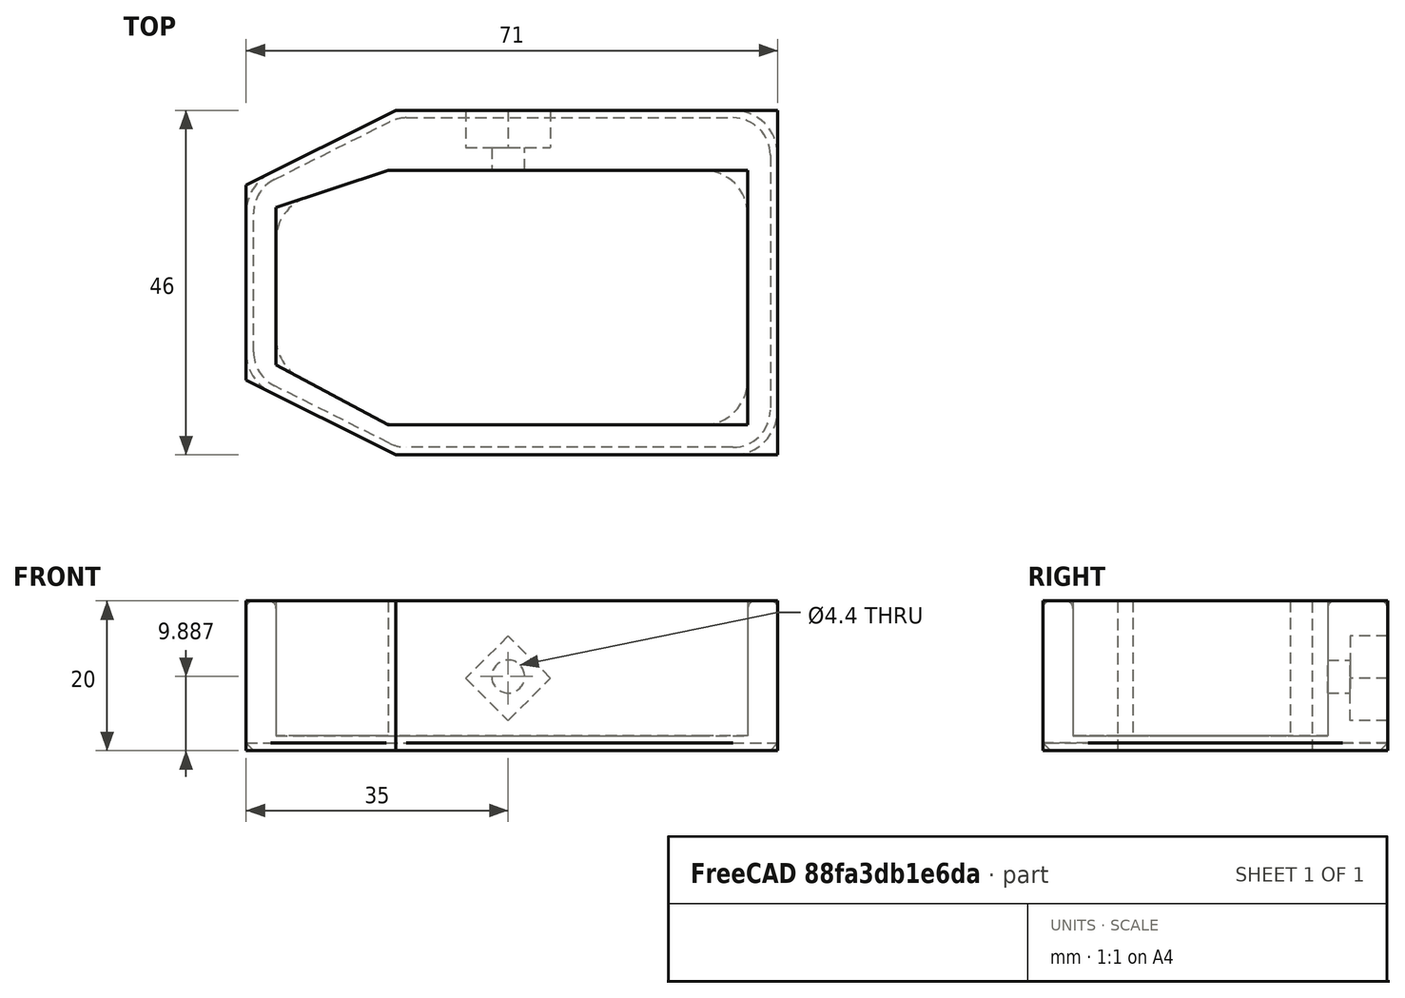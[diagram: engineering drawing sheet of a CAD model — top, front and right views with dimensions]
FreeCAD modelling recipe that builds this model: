
FCSTD DOCUMENT  (FreeCAD 0.16R)
Label: KetchupA
License: All rights reserved
LicenseURL: http://en.wikipedia.org/wiki/All_rights_reserved
objects: Sketcher::SketchObject×4, PartDesign::Pocket×3, PartDesign::Fillet×2, PartDesign::Pad×1, PartDesign::Chamfer×1, Mesh::Feature×1
note: 15 computed .brp shape members not serialized (recipe doc carries the construction recipe); baked Part::Feature solids carry a one-line shape summary decoded from their .brp

FEATURE [Sketcher::SketchObject] Sketch001
  sketch-geometry (6):
    g0: LineSegment StartX=-43 StartY=13 StartZ=0 EndX=-23 EndY=23 EndZ=0
    g1: LineSegment StartX=-23 StartY=23 StartZ=0 EndX=28 EndY=23 EndZ=0
    g2: LineSegment StartX=28 StartY=23 StartZ=0 EndX=28 EndY=-23 EndZ=0
    g3: LineSegment StartX=28 StartY=-23 StartZ=0 EndX=-23 EndY=-23 EndZ=0
    g4: LineSegment StartX=-23 StartY=-23 StartZ=0 EndX=-43 EndY=-13 EndZ=0
    g5: LineSegment StartX=-43 StartY=-13 StartZ=0 EndX=-43 EndY=13 EndZ=0
  constraints (18):
    c: Coincident(g0,g1)
    c: Horizontal(g1)
    c: Coincident(g1,g2)
    c: Vertical(g2)
    c: Coincident(g2,g3)
    c: Horizontal(g3)
    c: Coincident(g3,g4)
    c: Coincident(g4,g5)
    c: Coincident(g5,g0)
    c: Vertical(g5)
    c: Symmetric(g1,g2,g-1)
    c: Symmetric(g0,g4,g-1)
    c: DistanceX(g4) = -43
    c: DistanceX(g2) = 28
    c: Distance(g3,g0) = 46
    c: Equal(g1,g3)
    c: Distance(g5) = 26
    c: Distance(g3) = 51
FEATURE [PartDesign::Pad] Pad
  Length = 20
  Length2 = 100
  Sketch = -> Sketch001
  Type = 0
FEATURE [Sketcher::SketchObject] Sketch
  Placement = pos=(0,0,20) rot=(0,0,1;0rad)
  Support = -> Pad [Face8]
  sketch-geometry (6):
    g0: LineSegment StartX=-24 StartY=15 StartZ=0 EndX=24 EndY=15 EndZ=0
    g1: LineSegment StartX=24 StartY=15 StartZ=0 EndX=24 EndY=-19 EndZ=0
    g2: LineSegment StartX=24 StartY=-19 StartZ=0 EndX=-24 EndY=-19 EndZ=0
    g3: LineSegment StartX=-24 StartY=-19 StartZ=0 EndX=-39 EndY=-11 EndZ=0
    g4: LineSegment StartX=-39 StartY=-11 StartZ=0 EndX=-39 EndY=10 EndZ=0
    g5: LineSegment StartX=-39 StartY=10 StartZ=0 EndX=-24 EndY=15 EndZ=0
  constraints (18):
    c: Horizontal(g0)
    c: Coincident(g0,g1)
    c: Coincident(g1,g2)
    c: Horizontal(g2)
    c: Coincident(g2,g3)
    c: Coincident(g3,g4)
    c: Vertical(g4)
    c: Coincident(g4,g5)
    c: Coincident(g5,g0)
    c: Vertical(g1)
    c: Distance(g1) = 34
    c: Distance(g0) = 48
    c: Equal(g2,g0)
    c: DistanceX(g4,g0) = 15
    c: Distance(g4) = 21
    c: DistanceY(g1) = -19
    c: DistanceX(g1) = 24
    c: DistanceY(g3) = -11
FEATURE [PartDesign::Pocket] Pocket
  Length = 18
  Sketch = -> Sketch
  Type = 0
FEATURE [Sketcher::SketchObject] Sketch002
  Placement = pos=(0,23,0) rot=(0,0.707107,0.707107;3.14159rad)
  Support = -> Pocket [Face3]
  sketch-geometry (4):
    g0: LineSegment StartX=8.01225 StartY=15.3137 StartZ=0 EndX=13.6691 EndY=9.65685 EndZ=0
    g1: LineSegment StartX=13.6691 StartY=9.65685 StartZ=0 EndX=8.01225 EndY=4 EndZ=0
    g2: LineSegment StartX=8.01225 StartY=4 StartZ=0 EndX=2.3554 EndY=9.65685 EndZ=0
    g3: LineSegment StartX=2.3554 StartY=9.65685 StartZ=0 EndX=8.01225 EndY=15.3137 EndZ=0
  constraints (12):
    c: Coincident(g0,g1)
    c: Coincident(g1,g2)
    c: Coincident(g2,g3)
    c: Coincident(g3,g0)
    c: Equal(g1,g0)
    c: Distance(g1) = 8
    c: Equal(g3,g0)
    c: Equal(g1,g0)
    c: Perpendicular(g0,g3)
    c: Equal(g2,g1)
    c: DistanceY(g1) = 4
    c: Angle(g0) = -0.785398
FEATURE [PartDesign::Pocket] Pocket001
  Length = 5
  Sketch = -> Sketch002
  Type = 0
FEATURE [Sketcher::SketchObject] Sketch003
  Placement = pos=(0,18,0) rot=(0,0.707107,0.707107;3.14159rad)
  Support = -> Pocket001 [Face19]
  sketch-geometry (1):
    g0: Circle CenterX=8 CenterY=9.88737 CenterZ=0 NormalX=0 NormalY=0 NormalZ=1 Radius=2.2
  constraints (2):
    c: Radius(g0) = 2.2
    c: DistanceX(g0) = 8
FEATURE [PartDesign::Pocket] Pocket002
  Length = 5
  Sketch = -> Sketch003
  Type = 0
FEATURE [PartDesign::Fillet] Fillet
  Base = -> Pocket002 [Edge5,Edge1,Edge2,Edge41,Edge39,Edge37,Edge27,Edge28,Edge48,Edge45,Edge10,Edge43]
  Radius = 6
FEATURE [PartDesign::Fillet] Fillet001
  Base = -> Fillet [Edge4,Edge17,Edge19,Edge20,Edge21,Edge22,Edge23,Edge24,Edge25,Edge26,Edge27,Edge28,Edge29,Edge30,Edge31,Edge32,Edge33,Edge34,Edge35,Edge36,Edge37,Edge38,Edge39,Edge40]
  Radius = 1
FEATURE [PartDesign::Chamfer] Chamfer
  Base = -> Fillet001 [Edge3,Edge6,Edge11,Edge12,Edge13,Edge14,Edge15,Edge16,Edge17,Edge18,Edge19,Edge20]
  Size = 1
FEATURE [Mesh::Feature] Mesh  label="Chamfer (Meshed)"
